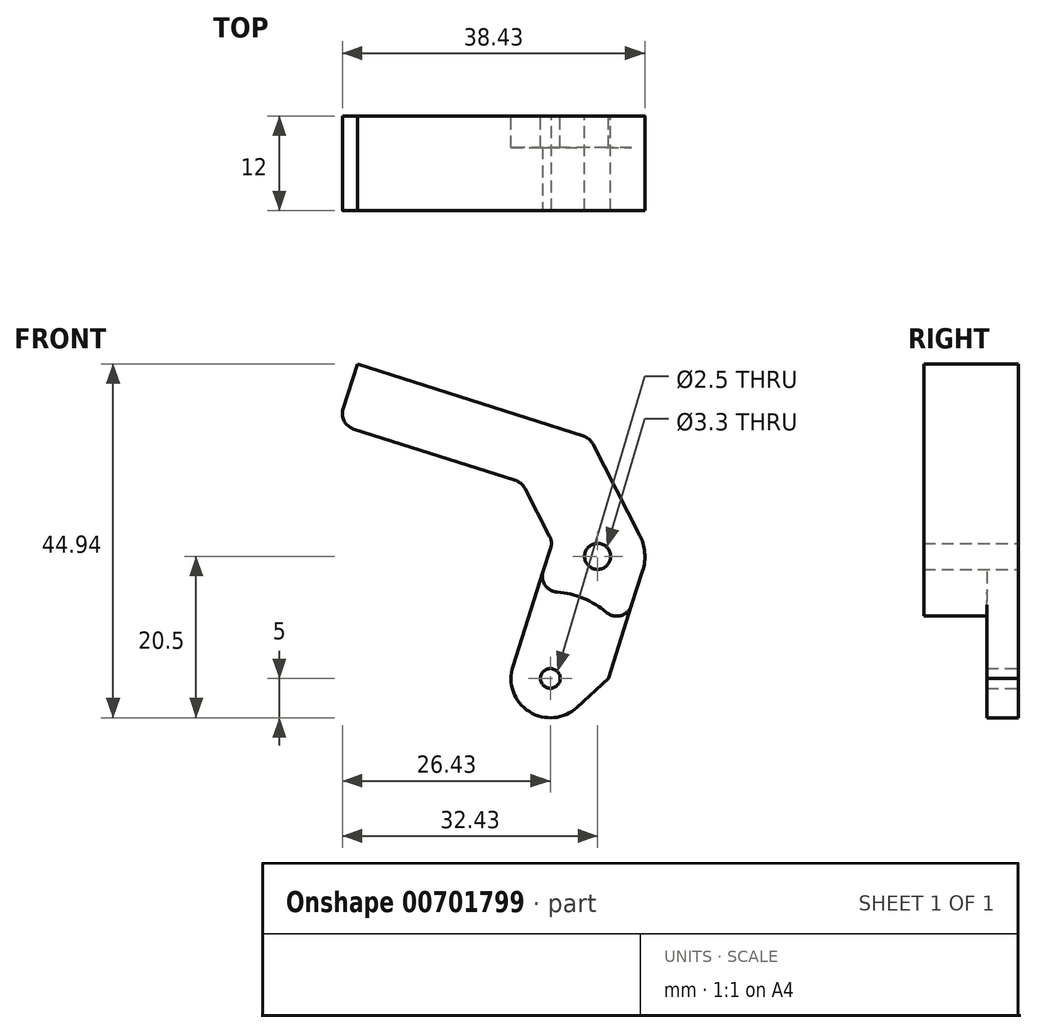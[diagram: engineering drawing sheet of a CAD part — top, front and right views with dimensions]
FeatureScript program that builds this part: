
annotation { "Feature Type Name" : "Feature", "Feature Type Description" : "" }
export const myFeature = defineFeature(function(context is Context, id is Id, definition is map)
    precondition{}
    {
        {
            var Q0;
            Q0=qCreatedBy(makeId("Front.planeOp"),FACE);
            var sketch = newSketch(context, id + "F0", { "sketchPlane" : qUnion([Q0])});
            skCircle(sketch, "E0", {"center": v(0, 0) * mm, "radius": 11.5 * mm, "construction": true});
            skCircle(sketch, "E1", {"center": v(-15.5, 15.5) * mm, "radius": 1.65 * mm, "construction": true});
            skCircle(sketch, "E2.1.0", {"center": v(-15.5, -15.5) * mm, "radius": 1.65 * mm, "construction": true});
            skCircle(sketch, "E2.2.0", {"center": v(15.5, -15.5) * mm, "radius": 1.65 * mm, "construction": true});
            skCircle(sketch, "E2.3.0", {"center": v(15.5, 15.5) * mm, "radius": 1.65 * mm, "construction": true});
            skCircle(sketch, "E3", {"center": v(0, 0) * mm, "radius": 4.5 * mm, "construction": true});
            skCircle(sketch, "E4", {"center": v(9.5, 0) * mm, "radius": 5 * mm});
            skCircle(sketch, "E5", {"center": v(15.5, 15.5) * mm, "radius": 6 * mm});
            skLineSegment(sketch, "E6", {"start": v(9.78, 17.33) * mm, "end": v(4.74, 1.52) * mm});
            skLineSegment(sketch, "E7", {"start": v(21.22, 13.67) * mm, "end": v(16.85, 0) * mm});
            skLineSegment(sketch, "E8", {"start": v(16.85, 0) * mm, "end": v(12.9, -3.66) * mm});
            skLineSegment(sketch, "E9", {"start": v(15.5, 15.5) * mm, "end": v(-8.98, 15.5) * mm});
            skLineSegment(sketch, "E10", {"start": v(-17.44, 32.32) * mm, "end": v(17.33, 21.22) * mm});
            skLineSegment(sketch, "E11", {"start": v(9.78, 17.33) * mm, "end": v(5.9, 24.87) * mm});
            skLineSegment(sketch, "E12", {"start": v(-17.44, 32.32) * mm, "end": v(-15.01, 39.94) * mm});
            skLineSegment(sketch, "E13", {"start": v(-15.01, 39.94) * mm, "end": v(14.5, 30.51) * mm});
            skLineSegment(sketch, "E14", {"start": v(14.5, 30.51) * mm, "end": v(20.83, 18.25) * mm});
            skCircle(sketch, "E15", {"center": v(15.5, 15.5) * mm, "radius": 1.65 * mm});
            skCircle(sketch, "E16", {"center": v(9.5, 0) * mm, "radius": 1.25 * mm});
            skSolve(sketch);
        }
        {
            var Q0;
            {var subQ0=sQuery(id+"F0.wireOp",EDGE,"E12");Q0=makeQuery(id+"F0.imprint","IMPRINT",FACE,{"disambiguationData":[TD([[makeQuery(id+"F0.imprint","IMPRINT",EDGE,{"derivedFrom":subQ0}),-1.0]])]});}
            var Q1;
            {var subQ0=sQuery(id+"F0.wireOp",EDGE,"E11");Q1=makeQuery(id+"F0.imprint","IMPRINT",FACE,{"disambiguationData":[TD([[makeQuery(id+"F0.imprint","IMPRINT",EDGE,{"derivedFrom":subQ0}),-1.0]])]});}
            var Q2;
            Q2=makeQuery(id+"F0.imprint","IMPRINT",FACE,{"disambiguationData":[TD([[makeQuery(id+"F0.imprint","IMPRINT",EDGE,{"derivedFrom":sQuery(id+"F0.wireOp",EDGE,"E15")}),-1.0]])]});
            var Q3;
            {var subQ0=sQuery(id+"F0.wireOp",EDGE,"E7");Q3=makeQuery(id+"F0.imprint","IMPRINT",FACE,{"disambiguationData":[TD([[makeQuery(id+"F0.imprint","IMPRINT",EDGE,{"derivedFrom":subQ0}),-1.0]])]});}
            var Q4;
            Q4=makeQuery(id+"F0.imprint","IMPRINT",FACE,{"disambiguationData":[TD([[makeQuery(id+"F0.imprint","IMPRINT",EDGE,{"derivedFrom":sQuery(id+"F0.wireOp",EDGE,"E16")}),-1.0]])]});
            var Q5;
            {var subQ0=sQuery(id+"F0.wireOp",EDGE,"E6");var subQ3=sQuery(id+"F0.wireOp",EDGE,"E9");var subQ5=makeQuery(id+"F0.imprint","INTERSECT",VERTEX,{"derivedFrom":[subQ0,subQ3]});Q5=makeQuery(id+"F0.imprint","IMPRINT",FACE,{"disambiguationData":[TD([[makeQuery(id+"F0.imprint","IMPRINT",EDGE,{"disambiguationData":[TD([[subQ5,1.0]])],"derivedFrom":subQ3}),-1.0]])]});}
            extrude(context, id + "F1", {"entities" : qUnion([Q0, Q1, Q2, Q3, Q4, Q5]), "depth" : 12 * mm, "offsetDistance" : 25 * mm});
        }
        {
            var Q0;
            Q0=makeQuery(id+"F1.opExtrude","CAP_FACE",FACE,{"disambiguationData":[OSD([sQuery(id+"F0.wireOp",EDGE,"E4"),sQuery(id+"F0.wireOp",EDGE,"E5"),sQuery(id+"F0.wireOp",EDGE,"E6"),sQuery(id+"F0.wireOp",EDGE,"E7"),sQuery(id+"F0.wireOp",EDGE,"E8"),sQuery(id+"F0.wireOp",EDGE,"E10"),sQuery(id+"F0.wireOp",EDGE,"E11"),sQuery(id+"F0.wireOp",EDGE,"E12"),sQuery(id+"F0.wireOp",EDGE,"E13"),sQuery(id+"F0.wireOp",EDGE,"E14"),sQuery(id+"F0.wireOp",EDGE,"E15"),sQuery(id+"F0.wireOp",EDGE,"E16")])],"isStart":false});
            var sketch = newSketch(context, id + "F2", { "sketchPlane" : qUnion([Q0])});
            skCircle(sketch, "E17.0", {"center": v(9.5, 0) * mm, "radius": 1.25 * mm});
            skCircle(sketch, "E18", {"center": v(9.5, 0) * mm, "radius": 11 * mm});
            skPoint(sketch, "E19.1.internal.snap0", {"position": v(-16.23, 36.13) * mm});
            skFitSpline(sketch, "E19", {"points": [v(-16.23, 36.13) * mm, v(-11.31, 36.13) * mm, v(-6.91, 37.35) * mm], "startDerivative": vector(9.82, -0.64) * mm, "endDerivative": vector(8.73, 3.14) * mm});
            skSolve(sketch);
        }
        {
            var Q0;
            Q0 = qSketchRegion(id + "F2", true);
            extrude(context, id + "F3", {"entities" : qUnion([Q0]), "operationType" : NewBodyOperationType.REMOVE, "oppositeDirection" : true, "depth" : 8 * mm, "offsetDistance" : 25 * mm});
        }
        {
            var Q0;
            Q0=makeQuery(id+"F1.opExtrude","SWEPT_EDGE",EDGE,{"disambiguationData":[OSD([sQuery(id+"F0.wireOp",EDGE,"E10"),sQuery(id+"F0.wireOp",EDGE,"E12")])]});
            var Q1;
            Q1=makeQuery(id+"F1.opExtrude","SWEPT_EDGE",EDGE,{"disambiguationData":[OSD([sQuery(id+"F0.wireOp",EDGE,"E10"),sQuery(id+"F0.wireOp",EDGE,"E11")])]});
            var Q2;
            Q2=makeQuery(id+"F1.opExtrude","SWEPT_EDGE",EDGE,{"disambiguationData":[OSD([sQuery(id+"F0.wireOp",EDGE,"E5"),sQuery(id+"F0.wireOp",EDGE,"E6"),sQuery(id+"F0.wireOp",EDGE,"E11")])]});
            var Q3;
            Q3=makeQuery(id+"F3.boolean.opBoolean","INTERSECT",EDGE,{"derivedFrom":[makeQuery(id+"F1.opExtrude","SWEPT_FACE",FACE,{"disambiguationData":[OSD([sQuery(id+"F0.wireOp",EDGE,"E6")])]}),makeQuery(id+"F3.opExtrude","SWEPT_FACE",FACE,{"disambiguationData":[OSD([sQuery(id+"F2.wireOp",EDGE,"E18")])]})]});
            var Q4;
            Q4=makeQuery(id+"F3.boolean.opBoolean","INTERSECT",EDGE,{"derivedFrom":[makeQuery(id+"F1.opExtrude","SWEPT_FACE",FACE,{"disambiguationData":[OSD([sQuery(id+"F0.wireOp",EDGE,"E7")])]}),makeQuery(id+"F3.opExtrude","SWEPT_FACE",FACE,{"disambiguationData":[OSD([sQuery(id+"F2.wireOp",EDGE,"E18")])]})]});
            var Q5;
            Q5=makeQuery(id+"F1.opExtrude","SWEPT_EDGE",EDGE,{"disambiguationData":[OSD([sQuery(id+"F0.wireOp",EDGE,"E13"),sQuery(id+"F0.wireOp",EDGE,"E14")])]});
            fillet(context, id + "F4", {"entities" : qUnion([Q0, Q1, Q2, Q3, Q4, Q5]), "radius" : 2 * mm, "tangentPropagation" : true, "allowEdgeOverflow" : false});
        }
    });
